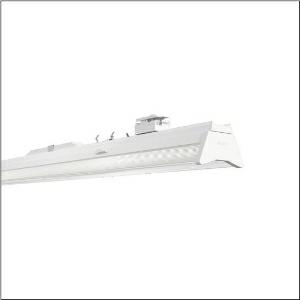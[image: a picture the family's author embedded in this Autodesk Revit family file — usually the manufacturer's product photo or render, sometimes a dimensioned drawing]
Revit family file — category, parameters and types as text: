
# Revit family: licross_r__21_performance_mo_52tm16cn445g_ee6e
name_source: partatom
category: Lighting Fixtures
units: mm (PartAtom-declared; Revit-internal decimal feet)

## family parameters
Cut with Voids When Loaded = No
Host = Face
Light Source = No
Part Type = Normal
Room Calculation Point = No
Round Connector Dimension = Use Diameter
Shared = No

## types (1)
- --- (1 x LED, 4500 lm, 24.1 W, 4000K)
    Apparent Load = 24 VA
    CIE Flux Codes = 66 88 96 79 100
    Color Rendering = 80
    Color Temperature = 4000K
    Default Elevation = 1800 mm
    Description = Licross® 21 Performance MO, luminaire insert, of sheet steel, galvanised, coil coated, white, length: 1.500mm, width: 120mm, height: 123mm, LED rated luminous flux: 4.500lm, light colour: 840, control gear: ON/OFF Multilumen, CLOi, control gear: ECG Multilumen, with plug, 3-pole, with phase selection, mains connection: 220..240V, AC, 50/60Hz, halogen-free wiring, primary light control with lens, of plastic, primary optical cover: cover, of PMMA, CAT 2 (L<= 3000cd/m²), light emission: direct/indirect distribution, primary light characteristic: symmetric, protection rating (complete): IP40, insulation class (complete): insulation class I (protective earthing), certification: CE, ENEC, UKCA, protection symbol: D if used in an environment without relevant dust loads with corresponding accessories, impact resistance: IK06, permissible ambient temperature for indoor applications: -35..+55°C, corresponds to IFS (International Featured Standards) requirements for safety and quality in the food industry, reducing of maximum allowable ambient temperature of 5°C with ceiling mounting, LABS conformity tested according to VDMA 24364:2018-05, packaging unit: 1 piece
    Height = 114 mm
    Lamp = 1 x LED
    Lamp Light Flux = 4500 lm
    Lamp Power = 24.1 W
    Lamp count = 1
    Length = 1500 mm
    Luminous efficacy = 187 lm/W
    Manufacturer = Siteco
    ModVariant = No
    Model = 52TM16CN445G
    Mounting Place = Ceiling
    Mounting Type = Pendant
    Number of Poles = 1
    OnlyDefault = Yes
    Power Factor = 1
    Product Name = Licross® 21 Performance MO
    Product group = luminaire insert
    ProductGroupID = 902
    Protection Class = Protection class I
    Protection Degree = IP 40
    RLX_Detail_Level = 1
    RlxData = <blob elided: 31365 chars, md5=4fa421a5>
    Socket = socket
    Standby Power = 0 W
    System Light Flux = 4500 lm
    System Power = 24 W
    Type Comments = factory setting: luminous flux: 100 % | (A | C | E) | 55 mA
    Type Image = l_1256138.jpg
    URL = http://relux.com
    VarID = @adj_004029
    Voltage = 0 V
    Weight = 0.00 kg
    Width = 120 mm

## geometry (parser evidence)
native form markers: Blend x4, Sweep x11
no freeform markers — native parametric forms only
